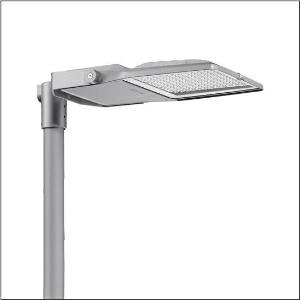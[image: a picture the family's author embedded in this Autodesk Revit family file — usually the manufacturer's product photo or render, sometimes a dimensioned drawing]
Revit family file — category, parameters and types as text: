
# Revit family: floodlight_fl_21_iq_midi___pl64_5xa7781f4e3a_1626
name_source: partatom
category: Lighting Fixtures
units: mm (PartAtom-declared; Revit-internal decimal feet)

## family parameters
Cut with Voids When Loaded = No
Host = Face
Light Source = No
Part Type = Normal
Room Calculation Point = No
Round Connector Dimension = Use Diameter
Shared = No

## types (1)
- --- (1 x LED, 36050 lm, 270.2 W, 4000K)
    Apparent Load = 270 VA
    CIE Flux Codes = 28 80 98 100 100
    Color Rendering = 70
    Color Temperature = 4000K
    Default Elevation = 1800 mm
    Description = Floodlight FL 21 iQ midi, floodlight, primary light control with lens, of PMMA, primary optical cover: protective disc, of toughened safety glass, transparent, light distribution: PL64, light emission: direct distribution, installation type: surface-mounted, LED, High Power LED, rated luminous flux: 36.050lm, luminous efficacy: 133lm/W, light colour: 740, colour temperature: 4000K, control gear: ECG iQ, control: optimised constant luminous flux control (CLO 2.0), Desk-Remote (wireless, voltage-free reading and setting of iQ features in the workshop via application-optimized NFC function/RFID function), Light-Fading, Smart-Wire, Night-Set, Lumen-Switch, Temp-Guard, Auto-Match, with terminal, 6-pole, mains connection: 220..240V, AC, 50/60Hz, start of lifetime: 270W, end of service life: 287W, reduction: 118W, luminaire housing, of diecast aluminium, powder-coated, Siteco® metallic grey (DB 702S), corrosivity category C5 mid according to DIN EN ISO 12944, sealing non-destructively replaceable, please order mast flange separately, mast bracket, of steel, galvanised, powder-coated, Siteco® metallic grey (DB 702S), protection rating (complete): IP66, insulation class (complete): insulation class II (safety insulation), certification: CE, protection symbol: D, impact resistance: IK08, permissible operating ambient temperature: -40..+40°C, permissible operating ambient temperature for outdoor applications: -40..+50°C, standard: DIN EN 12944, LABS conformity tested according to VDMA 24364:2018-05, packaging unit: 1 piece

Light Distribution: PL64
    Height = 76 mm
    Lamp = 1 x LED
    Lamp Light Flux = 36050 lm
    Lamp Power = 270.2 W
    Lamp count = 1
    Length = 657 mm
    Luminous efficacy = 133 lm/W
    Manufacturer = Siteco
    ModVariant = No
    Model = 5XA7781F4E3A
    Number of Poles = 1
    OnlyDefault = Yes
    Power Factor = 1
    Product Name = Floodlight FL 21 iQ midi | PL64
    Product group = floodlight | pylon annexe
    ProductGroupID = 6200
    Protection Class = Protection class II
    Protection Degree = IP 66
    RLX_Detail_Level = 1
    RLX_Emergency_Light_Flux = 0 lm
    RLX_Emergency_Type = 0
    RLX_Emergency_Type_DB = No
    RlxData = <blob elided: 153665 chars, md5=35f8ea1f>
    Socket = socket
    Standby Power = 0 W
    System Light Flux = 36050 lm
    System Power = 270 W
    Type Comments = factory setting: luminous flux: 100 % | dim-lin: 254 | 620 mA
    Type Image = l_1007123.jpg
    URL = http://relux.com
    VarID = @adj_036919
    Voltage = 0 V
    Weight = 0.00 kg
    Width = 442 mm

## geometry (parser evidence)
native form markers: Blend x4, Sweep x13
no freeform markers — native parametric forms only
